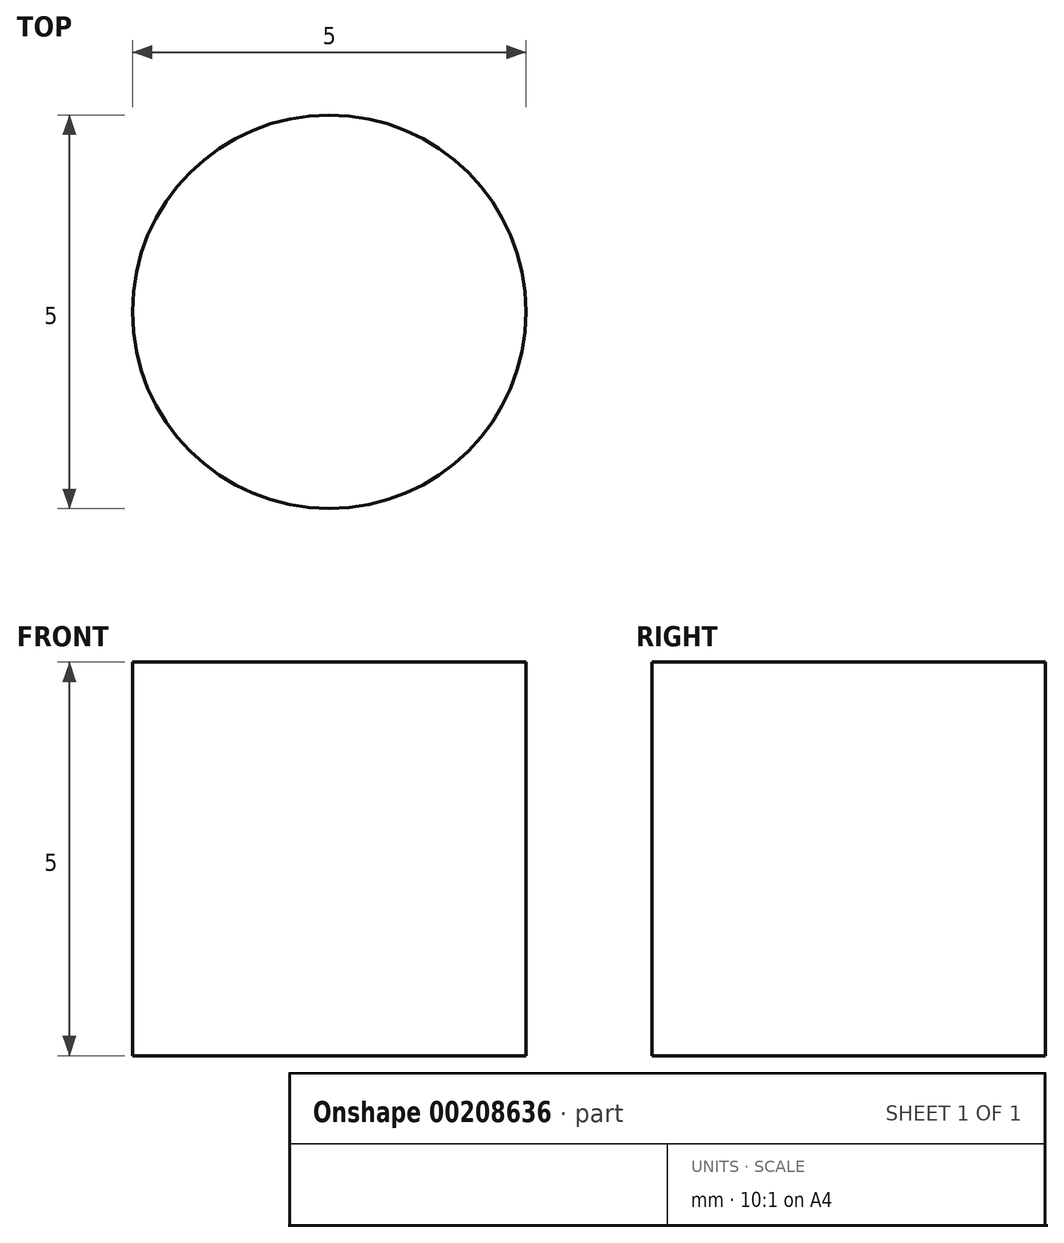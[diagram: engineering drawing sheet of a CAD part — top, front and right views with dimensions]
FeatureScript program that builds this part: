
annotation { "Feature Type Name" : "Feature", "Feature Type Description" : "" }
export const myFeature = defineFeature(function(context is Context, id is Id, definition is map)
    precondition{}
    {
        {
            var Q0;
            Q0=qCreatedBy(makeId("Top.planeOp"),FACE);
            var sketch = newSketch(context, id + "F0", { "sketchPlane" : qUnion([Q0])});
            skCircle(sketch, "E0", {"center": v(0, 0) * mm, "radius": 2.5 * mm});
            skSolve(sketch);
        }
        {
            var Q0;
            Q0=makeQuery(id+"F0.imprint","IMPRINT",FACE,{"disambiguationData":[TD([[makeQuery(id+"F0.imprint","IMPRINT",EDGE,{"derivedFrom":sQuery(id+"F0.wireOp",EDGE,"E0")}),1.0]])]});
            var Q1;
            Q1=sQuery(id+"F0.wireOp",EDGE,"E0");
            extrude(context, id + "F1", {"entities" : qUnion([Q0]), "surfaceEntities" : qUnion([Q1]), "depth" : 5 * mm});
        }
    });
